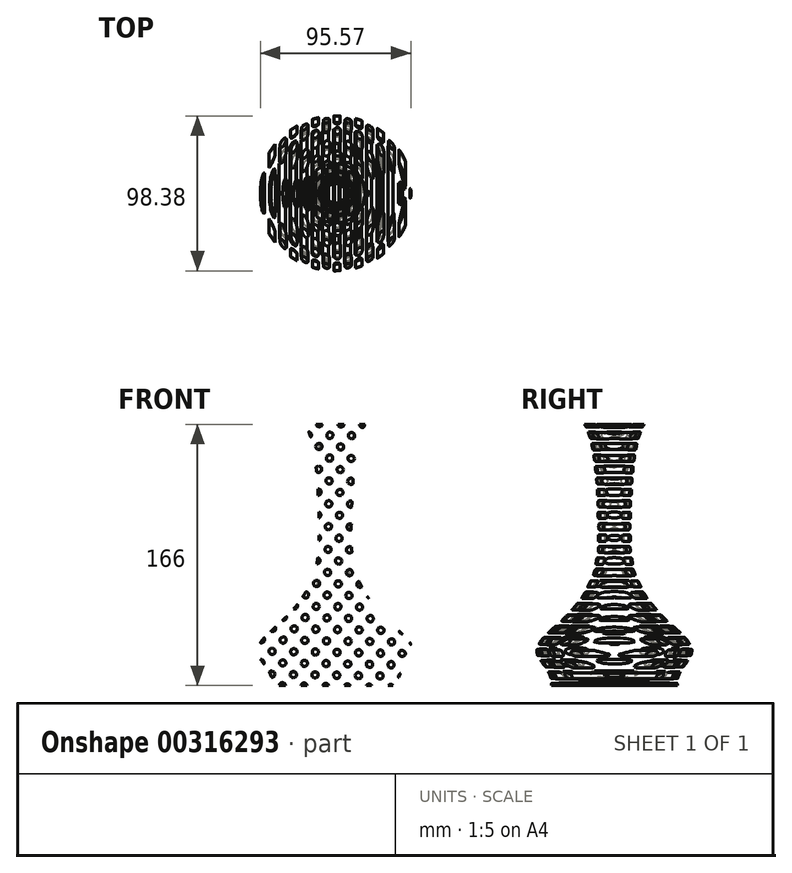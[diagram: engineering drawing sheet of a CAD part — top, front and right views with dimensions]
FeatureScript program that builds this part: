
annotation { "Feature Type Name" : "Feature", "Feature Type Description" : "" }
export const myFeature = defineFeature(function(context is Context, id is Id, definition is map)
    precondition{}
    {
        {
            var Q0;
            Q0=qCreatedBy(makeId("Top.planeOp"),FACE);
            var sketch = newSketch(context, id + "F0", { "sketchPlane" : qUnion([Q0])});
            skCircle(sketch, "E0", {"center": v(0, 0) * mm, "radius": 40 * mm});
            skSolve(sketch);
        }
        {
            var Q0;
            Q0=makeQuery(id+"F0.imprint","IMPRINT",FACE,{"disambiguationData":[TD([[makeQuery(id+"F0.imprint","IMPRINT",EDGE,{"derivedFrom":sQuery(id+"F0.wireOp",EDGE,"E0")}),1.0]])]});
            cPlane(context, id + "F1", {"entities" : qUnion([Q0]), "cplaneType" : CPlaneType.OFFSET, "offset" : 4 * mm, "width" : 150 * mm, "height" : 150 * mm});
        }
        {
            var Q0;
            Q0=qCreatedBy(id+"F1.planeOp",FACE);
            var sketch = newSketch(context, id + "F2", { "sketchPlane" : qUnion([Q0])});
            skCircle(sketch, "E1", {"center": v(0, 0) * mm, "radius": 41.51 * mm});
            skSolve(sketch);
        }
        {
            var Q0;
            Q0=makeQuery(id+"F2.imprint","IMPRINT",FACE,{"disambiguationData":[TD([[makeQuery(id+"F2.imprint","IMPRINT",EDGE,{"derivedFrom":sQuery(id+"F2.wireOp",EDGE,"E1")}),1.0]])]});
            cPlane(context, id + "F3", {"entities" : qUnion([Q0]), "cplaneType" : CPlaneType.OFFSET, "offset" : 6 * mm, "width" : 150 * mm, "height" : 150 * mm});
        }
        {
            var Q0;
            Q0=qCreatedBy(id+"F3.planeOp",FACE);
            var sketch = newSketch(context, id + "F4", { "sketchPlane" : qUnion([Q0])});
            skCircle(sketch, "E2", {"center": v(0, 0) * mm, "radius": 45.5 * mm});
            skSolve(sketch);
        }
        {
            var Q0;
            Q0=makeQuery(id+"F4.imprint","IMPRINT",FACE,{"disambiguationData":[TD([[makeQuery(id+"F4.imprint","IMPRINT",EDGE,{"derivedFrom":sQuery(id+"F4.wireOp",EDGE,"E2")}),1.0]])]});
            cPlane(context, id + "F5", {"entities" : qUnion([Q0]), "cplaneType" : CPlaneType.OFFSET, "offset" : 8 * mm, "width" : 150 * mm, "height" : 150 * mm});
        }
        {
            var Q0;
            Q0=qCreatedBy(id+"F5.planeOp",FACE);
            var sketch = newSketch(context, id + "F6", { "sketchPlane" : qUnion([Q0])});
            skCircle(sketch, "E3", {"center": v(0, 0) * mm, "radius": 49.2 * mm});
            skSolve(sketch);
        }
        {
            var Q0;
            Q0=makeQuery(id+"F6.imprint","IMPRINT",FACE,{"disambiguationData":[TD([[makeQuery(id+"F6.imprint","IMPRINT",EDGE,{"derivedFrom":sQuery(id+"F6.wireOp",EDGE,"E3")}),1.0]])]});
            cPlane(context, id + "F7", {"entities" : qUnion([Q0]), "cplaneType" : CPlaneType.OFFSET, "offset" : 6 * mm, "width" : 150 * mm, "height" : 150 * mm});
        }
        {
            var Q0;
            Q0=qCreatedBy(id+"F7.planeOp",FACE);
            var sketch = newSketch(context, id + "F8", { "sketchPlane" : qUnion([Q0])});
            skCircle(sketch, "E4", {"center": v(0, 0) * mm, "radius": 47 * mm});
            skSolve(sketch);
        }
        {
            var Q0;
            Q0=qCreatedBy(id+"F7.planeOp",FACE);
            cPlane(context, id + "F9", {"entities" : qUnion([Q0]), "cplaneType" : CPlaneType.OFFSET, "offset" : 6 * mm, "width" : 150 * mm, "height" : 150 * mm});
        }
        {
            var Q0;
            Q0=qCreatedBy(id+"F9.planeOp",FACE);
            var sketch = newSketch(context, id + "F10", { "sketchPlane" : qUnion([Q0])});
            skCircle(sketch, "E5", {"center": v(0, 0) * mm, "radius": 41.44 * mm});
            skSolve(sketch);
        }
        {
            var Q0;
            Q0=qCreatedBy(id+"F9.planeOp",FACE);
            cPlane(context, id + "F11", {"entities" : qUnion([Q0]), "cplaneType" : CPlaneType.OFFSET, "offset" : 16 * mm, "width" : 150 * mm, "height" : 150 * mm});
        }
        {
            var Q0;
            Q0=qCreatedBy(id+"F11.planeOp",FACE);
            var sketch = newSketch(context, id + "F12", { "sketchPlane" : qUnion([Q0])});
            skCircle(sketch, "E6", {"center": v(0, 0) * mm, "radius": 25.29 * mm});
            skSolve(sketch);
        }
        {
            var Q0;
            Q0=qCreatedBy(id+"F11.planeOp",FACE);
            cPlane(context, id + "F13", {"entities" : qUnion([Q0]), "cplaneType" : CPlaneType.OFFSET, "offset" : 25 * mm, "width" : 150 * mm, "height" : 150 * mm});
        }
        {
            var Q0;
            Q0=qCreatedBy(id+"F13.planeOp",FACE);
            var sketch = newSketch(context, id + "F14", { "sketchPlane" : qUnion([Q0])});
            skCircle(sketch, "E7", {"center": v(0, 0) * mm, "radius": 12.22 * mm});
            skSolve(sketch);
        }
        {
            var Q0;
            Q0=qCreatedBy(id+"F13.planeOp",FACE);
            cPlane(context, id + "F15", {"entities" : qUnion([Q0]), "cplaneType" : CPlaneType.OFFSET, "offset" : 25 * mm, "width" : 150 * mm, "height" : 150 * mm});
        }
        {
            var Q0;
            Q0=qCreatedBy(id+"F15.planeOp",FACE);
            var sketch = newSketch(context, id + "F16", { "sketchPlane" : qUnion([Q0])});
            skCircle(sketch, "E8", {"center": v(0, 0) * mm, "radius": 10.18 * mm});
            skSolve(sketch);
        }
        {
            var Q0;
            Q0=qCreatedBy(id+"F15.planeOp",FACE);
            cPlane(context, id + "F17", {"entities" : qUnion([Q0]), "cplaneType" : CPlaneType.OFFSET, "offset" : 25 * mm, "width" : 150 * mm, "height" : 150 * mm});
        }
        {
            var Q0;
            Q0=qCreatedBy(id+"F17.planeOp",FACE);
            var sketch = newSketch(context, id + "F18", { "sketchPlane" : qUnion([Q0])});
            skCircle(sketch, "E9", {"center": v(0, 0) * mm, "radius": 11 * mm});
            skSolve(sketch);
        }
        {
            var Q0;
            Q0=qCreatedBy(id+"F17.planeOp",FACE);
            cPlane(context, id + "F19", {"entities" : qUnion([Q0]), "cplaneType" : CPlaneType.OFFSET, "offset" : 25 * mm, "width" : 150 * mm, "height" : 150 * mm});
        }
        {
            var Q0;
            Q0=qCreatedBy(id+"F19.planeOp",FACE);
            var sketch = newSketch(context, id + "F20", { "sketchPlane" : qUnion([Q0])});
            skCircle(sketch, "E10", {"center": v(0, 0) * mm, "radius": 13.75 * mm});
            skSolve(sketch);
        }
        {
            var Q0;
            Q0=qCreatedBy(id+"F19.planeOp",FACE);
            cPlane(context, id + "F21", {"entities" : qUnion([Q0]), "cplaneType" : CPlaneType.OFFSET, "offset" : 10 * mm, "width" : 150 * mm, "height" : 150 * mm});
        }
        {
            var Q0;
            Q0=qCreatedBy(id+"F21.planeOp",FACE);
            var sketch = newSketch(context, id + "F22", { "sketchPlane" : qUnion([Q0])});
            skCircle(sketch, "E11", {"center": v(0, 0) * mm, "radius": 16.33 * mm});
            skSolve(sketch);
        }
        {
            var Q0;
            Q0=qCreatedBy(id+"F21.planeOp",FACE);
            cPlane(context, id + "F23", {"entities" : qUnion([Q0]), "cplaneType" : CPlaneType.OFFSET, "offset" : 6 * mm, "width" : 150 * mm, "height" : 150 * mm});
        }
        {
            var Q0;
            Q0=qCreatedBy(id+"F23.planeOp",FACE);
            var sketch = newSketch(context, id + "F24", { "sketchPlane" : qUnion([Q0])});
            skCircle(sketch, "E12", {"center": v(0, 0) * mm, "radius": 18.94 * mm});
            skSolve(sketch);
        }
        {
            var Q0;
            Q0=qSketchRegion(id+"F0",true);
            var Q1;
            Q1=qSketchRegion(id+"F2",true);
            var Q2;
            Q2=qSketchRegion(id+"F4",true);
            var Q3;
            Q3=qSketchRegion(id+"F6",true);
            var Q4;
            Q4=qSketchRegion(id+"F8",true);
            var Q5;
            Q5=qSketchRegion(id+"F10",true);
            var Q6;
            Q6=qSketchRegion(id+"F12",true);
            var Q7;
            Q7=qSketchRegion(id+"F14",true);
            var Q8;
            Q8=qSketchRegion(id+"F16",true);
            var Q9;
            Q9=qSketchRegion(id+"F18",true);
            var Q10;
            Q10=qSketchRegion(id+"F20",true);
            var Q11;
            Q11=qSketchRegion(id+"F22",true);
            var Q12;
            Q12=qSketchRegion(id+"F24",true);
            loft(context, id + "F25", {"sheetProfilesArray" : [{ "sheetProfileEntities" : qUnion([Q0]) }, { "sheetProfileEntities" : qUnion([Q1]) }, { "sheetProfileEntities" : qUnion([Q2]) }, { "sheetProfileEntities" : qUnion([Q3]) }, { "sheetProfileEntities" : qUnion([Q4]) }, { "sheetProfileEntities" : qUnion([Q5]) }, { "sheetProfileEntities" : qUnion([Q6]) }, { "sheetProfileEntities" : qUnion([Q7]) }, { "sheetProfileEntities" : qUnion([Q8]) }, { "sheetProfileEntities" : qUnion([Q9]) }, { "sheetProfileEntities" : qUnion([Q10]) }, { "sheetProfileEntities" : qUnion([Q11]) }, { "sheetProfileEntities" : qUnion([Q12]) }]});
        }
        {
            var Q0;
            Q0=makeQuery(id+"F25.opLoft","CAP_FACE",FACE,{"disambiguationData":[OSD([makeQuery(id+"F24.imprint","IMPRINT",FACE,{"disambiguationData":[TD([[makeQuery(id+"F24.imprint","IMPRINT",EDGE,{"derivedFrom":sQuery(id+"F24.wireOp",EDGE,"E12")}),1.0]])]})])],"isStart":true});
            shell(context, id + "F26", {"entities" : qUnion([Q0]), "thickness" : 4 * mm});
        }
        {
            var Q0;
            Q0=qCreatedBy(makeId("Top.planeOp"),FACE);
            var sketch = newSketch(context, id + "F27", { "sketchPlane" : qUnion([Q0])});
            skCircle(sketch, "E13", {"center": v(0, 0) * mm, "radius": 40.24 * mm});
            skSolve(sketch);
        }
        {
            var Q0;
            Q0=qSketchRegion(id+"F27",true);
            extrude(context, id + "F28", {"entities" : qUnion([Q0]), "operationType" : NewBodyOperationType.ADD, "oppositeDirection" : true, "depth" : 4 * mm});
        }
        {
            var Q0;
            Q0=qCreatedBy(makeId("Front.planeOp"),FACE);
            var sketch = newSketch(context, id + "F29", { "sketchPlane" : qUnion([Q0])});
            skCircle(sketch, "E14", {"center": v(0, -55.44) * mm, "radius": 2 * mm});
            skCircle(sketch, "E15.0.1.0", {"center": v(-6.76, -48.08) * mm, "radius": 2 * mm});
            skCircle(sketch, "E15.0.2.0", {"center": v(-13.52, -40.7) * mm, "radius": 2 * mm});
            skCircle(sketch, "E15.0.3.0", {"center": v(-20.28, -33.34) * mm, "radius": 2 * mm});
            skCircle(sketch, "E15.0.4.0", {"center": v(-27.04, -25.97) * mm, "radius": 2 * mm});
            skCircle(sketch, "E15.0.5.0", {"center": v(-33.8, -18.6) * mm, "radius": 2 * mm});
            skCircle(sketch, "E15.0.6.0", {"center": v(-40.56, -11.23) * mm, "radius": 2 * mm});
            skCircle(sketch, "E15.0.7.0", {"center": v(-47.32, -3.86) * mm, "radius": 2 * mm});
            skCircle(sketch, "E15.0.8.0", {"center": v(-54.07, 3.51) * mm, "radius": 2 * mm});
            skCircle(sketch, "E15.0.9.0", {"center": v(-60.83, 10.88) * mm, "radius": 2 * mm});
            skCircle(sketch, "E15.0.10.0", {"center": v(-67.6, 18.25) * mm, "radius": 2 * mm});
            skCircle(sketch, "E15.0.11.0", {"center": v(-74.35, 25.62) * mm, "radius": 2 * mm});
            skCircle(sketch, "E15.0.12.0", {"center": v(-81.11, 33) * mm, "radius": 2 * mm});
            skCircle(sketch, "E15.0.13.0", {"center": v(-87.87, 40.36) * mm, "radius": 2 * mm});
            skCircle(sketch, "E15.0.14.0", {"center": v(-94.63, 47.73) * mm, "radius": 2 * mm});
            skCircle(sketch, "E15.0.15.0", {"center": v(-101.39, 55.1) * mm, "radius": 2 * mm});
            skCircle(sketch, "E15.0.16.0", {"center": v(-108.15, 62.47) * mm, "radius": 2 * mm});
            skCircle(sketch, "E15.0.17.0", {"center": v(-114.9, 69.84) * mm, "radius": 2 * mm});
            skCircle(sketch, "E15.0.18.0", {"center": v(-121.67, 77.2) * mm, "radius": 2 * mm});
            skCircle(sketch, "E15.0.19.0", {"center": v(-128.43, 84.58) * mm, "radius": 2 * mm});
            skCircle(sketch, "E15.0.20.0", {"center": v(-135.19, 91.95) * mm, "radius": 2 * mm});
            skCircle(sketch, "E15.0.21.0", {"center": v(-141.95, 99.32) * mm, "radius": 2 * mm});
            skCircle(sketch, "E15.0.22.0", {"center": v(-148.7, 106.69) * mm, "radius": 2 * mm});
            skCircle(sketch, "E15.0.23.0", {"center": v(-155.46, 114.06) * mm, "radius": 2 * mm});
            skCircle(sketch, "E15.0.24.0", {"center": v(-162.22, 121.43) * mm, "radius": 2 * mm});
            skCircle(sketch, "E15.1.0.0", {"center": v(7, -48.3) * mm, "radius": 2 * mm});
            skCircle(sketch, "E15.1.1.0", {"center": v(0.24, -40.94) * mm, "radius": 2 * mm});
            skCircle(sketch, "E15.1.2.0", {"center": v(-6.52, -33.57) * mm, "radius": 2 * mm});
            skCircle(sketch, "E15.1.3.0", {"center": v(-13.27, -26.2) * mm, "radius": 2 * mm});
            skCircle(sketch, "E15.1.4.0", {"center": v(-20.03, -18.83) * mm, "radius": 2 * mm});
            skCircle(sketch, "E15.1.5.0", {"center": v(-26.8, -11.46) * mm, "radius": 2 * mm});
            skCircle(sketch, "E15.1.6.0", {"center": v(-33.55, -4.09) * mm, "radius": 2 * mm});
            skCircle(sketch, "E15.1.7.0", {"center": v(-40.31, 3.28) * mm, "radius": 2 * mm});
            skCircle(sketch, "E15.1.8.0", {"center": v(-47.07, 10.65) * mm, "radius": 2 * mm});
            skCircle(sketch, "E15.1.9.0", {"center": v(-53.83, 18.02) * mm, "radius": 2 * mm});
            skCircle(sketch, "E15.1.10.0", {"center": v(-60.6, 25.4) * mm, "radius": 2 * mm});
            skCircle(sketch, "E15.1.11.0", {"center": v(-67.35, 32.76) * mm, "radius": 2 * mm});
            skCircle(sketch, "E15.1.12.0", {"center": v(-74.1, 40.13) * mm, "radius": 2 * mm});
            skCircle(sketch, "E15.1.13.0", {"center": v(-80.87, 47.5) * mm, "radius": 2 * mm});
            skCircle(sketch, "E15.1.14.0", {"center": v(-87.63, 54.87) * mm, "radius": 2 * mm});
            skCircle(sketch, "E15.1.15.0", {"center": v(-94.39, 62.24) * mm, "radius": 2 * mm});
            skCircle(sketch, "E15.1.16.0", {"center": v(-101.15, 69.6) * mm, "radius": 2 * mm});
            skCircle(sketch, "E15.1.17.0", {"center": v(-107.9, 76.98) * mm, "radius": 2 * mm});
            skCircle(sketch, "E15.1.18.0", {"center": v(-114.66, 84.35) * mm, "radius": 2 * mm});
            skCircle(sketch, "E15.1.19.0", {"center": v(-121.42, 91.72) * mm, "radius": 2 * mm});
            skCircle(sketch, "E15.1.20.0", {"center": v(-128.18, 99.09) * mm, "radius": 2 * mm});
            skCircle(sketch, "E15.1.21.0", {"center": v(-134.94, 106.46) * mm, "radius": 2 * mm});
            skCircle(sketch, "E15.1.22.0", {"center": v(-141.7, 113.83) * mm, "radius": 2 * mm});
            skCircle(sketch, "E15.1.23.0", {"center": v(-148.46, 121.2) * mm, "radius": 2 * mm});
            skCircle(sketch, "E15.1.24.0", {"center": v(-155.22, 128.57) * mm, "radius": 2 * mm});
            skCircle(sketch, "E15.2.0.0", {"center": v(14, -41.17) * mm, "radius": 2 * mm});
            skCircle(sketch, "E15.2.1.0", {"center": v(7.25, -33.8) * mm, "radius": 2 * mm});
            skCircle(sketch, "E15.2.2.0", {"center": v(0.49, -26.43) * mm, "radius": 2 * mm});
            skCircle(sketch, "E15.2.3.0", {"center": v(-6.27, -19.06) * mm, "radius": 2 * mm});
            skCircle(sketch, "E15.2.4.0", {"center": v(-13.03, -11.69) * mm, "radius": 2 * mm});
            skCircle(sketch, "E15.2.5.0", {"center": v(-19.8, -4.32) * mm, "radius": 2 * mm});
            skCircle(sketch, "E15.2.6.0", {"center": v(-26.55, 3.05) * mm, "radius": 2 * mm});
            skCircle(sketch, "E15.2.7.0", {"center": v(-33.3, 10.42) * mm, "radius": 2 * mm});
            skCircle(sketch, "E15.2.8.0", {"center": v(-40.07, 17.79) * mm, "radius": 2 * mm});
            skCircle(sketch, "E15.2.9.0", {"center": v(-46.83, 25.16) * mm, "radius": 2 * mm});
            skCircle(sketch, "E15.2.10.0", {"center": v(-53.59, 32.53) * mm, "radius": 2 * mm});
            skCircle(sketch, "E15.2.11.0", {"center": v(-60.35, 39.9) * mm, "radius": 2 * mm});
            skCircle(sketch, "E15.2.12.0", {"center": v(-67.1, 47.27) * mm, "radius": 2 * mm});
            skCircle(sketch, "E15.2.13.0", {"center": v(-73.86, 54.64) * mm, "radius": 2 * mm});
            skCircle(sketch, "E15.2.14.0", {"center": v(-80.62, 62) * mm, "radius": 2 * mm});
            skCircle(sketch, "E15.2.15.0", {"center": v(-87.38, 69.38) * mm, "radius": 2 * mm});
            skCircle(sketch, "E15.2.16.0", {"center": v(-94.14, 76.75) * mm, "radius": 2 * mm});
            skCircle(sketch, "E15.2.17.0", {"center": v(-100.9, 84.12) * mm, "radius": 2 * mm});
            skCircle(sketch, "E15.2.18.0", {"center": v(-107.66, 91.49) * mm, "radius": 2 * mm});
            skCircle(sketch, "E15.2.19.0", {"center": v(-114.42, 98.86) * mm, "radius": 2 * mm});
            skCircle(sketch, "E15.2.20.0", {"center": v(-121.18, 106.23) * mm, "radius": 2 * mm});
            skCircle(sketch, "E15.2.21.0", {"center": v(-127.94, 113.6) * mm, "radius": 2 * mm});
            skCircle(sketch, "E15.2.22.0", {"center": v(-134.7, 120.96) * mm, "radius": 2 * mm});
            skCircle(sketch, "E15.2.23.0", {"center": v(-141.46, 128.33) * mm, "radius": 2 * mm});
            skCircle(sketch, "E15.2.24.0", {"center": v(-148.22, 135.7) * mm, "radius": 2 * mm});
            skCircle(sketch, "E15.3.0.0", {"center": v(21, -34.03) * mm, "radius": 2 * mm});
            skCircle(sketch, "E15.3.1.0", {"center": v(14.25, -26.66) * mm, "radius": 2 * mm});
            skCircle(sketch, "E15.3.2.0", {"center": v(7.5, -19.3) * mm, "radius": 2 * mm});
            skCircle(sketch, "E15.3.3.0", {"center": v(0.73, -11.92) * mm, "radius": 2 * mm});
            skCircle(sketch, "E15.3.4.0", {"center": v(-6.03, -4.55) * mm, "radius": 2 * mm});
            skCircle(sketch, "E15.3.5.0", {"center": v(-12.79, 2.82) * mm, "radius": 2 * mm});
            skCircle(sketch, "E15.3.6.0", {"center": v(-19.55, 10.19) * mm, "radius": 2 * mm});
            skCircle(sketch, "E15.3.7.0", {"center": v(-26.3, 17.56) * mm, "radius": 2 * mm});
            skCircle(sketch, "E15.3.8.0", {"center": v(-33.07, 24.93) * mm, "radius": 2 * mm});
            skCircle(sketch, "E15.3.9.0", {"center": v(-39.82, 32.3) * mm, "radius": 2 * mm});
            skCircle(sketch, "E15.3.10.0", {"center": v(-46.58, 39.67) * mm, "radius": 2 * mm});
            skCircle(sketch, "E15.3.11.0", {"center": v(-53.34, 47.04) * mm, "radius": 2 * mm});
            skCircle(sketch, "E15.3.12.0", {"center": v(-60.1, 54.4) * mm, "radius": 2 * mm});
            skCircle(sketch, "E15.3.13.0", {"center": v(-66.86, 61.78) * mm, "radius": 2 * mm});
            skCircle(sketch, "E15.3.14.0", {"center": v(-73.62, 69.15) * mm, "radius": 2 * mm});
            skCircle(sketch, "E15.3.15.0", {"center": v(-80.38, 76.52) * mm, "radius": 2 * mm});
            skCircle(sketch, "E15.3.16.0", {"center": v(-87.14, 83.89) * mm, "radius": 2 * mm});
            skCircle(sketch, "E15.3.17.0", {"center": v(-93.9, 91.25) * mm, "radius": 2 * mm});
            skCircle(sketch, "E15.3.18.0", {"center": v(-100.66, 98.62) * mm, "radius": 2 * mm});
            skCircle(sketch, "E15.3.19.0", {"center": v(-107.42, 106) * mm, "radius": 2 * mm});
            skCircle(sketch, "E15.3.20.0", {"center": v(-114.18, 113.36) * mm, "radius": 2 * mm});
            skCircle(sketch, "E15.3.21.0", {"center": v(-120.94, 120.73) * mm, "radius": 2 * mm});
            skCircle(sketch, "E15.3.22.0", {"center": v(-127.7, 128.1) * mm, "radius": 2 * mm});
            skCircle(sketch, "E15.3.23.0", {"center": v(-134.45, 135.47) * mm, "radius": 2 * mm});
            skCircle(sketch, "E15.3.24.0", {"center": v(-141.21, 142.84) * mm, "radius": 2 * mm});
            skCircle(sketch, "E15.4.0.0", {"center": v(28.01, -26.9) * mm, "radius": 2 * mm});
            skCircle(sketch, "E15.4.1.0", {"center": v(21.25, -19.52) * mm, "radius": 2 * mm});
            skCircle(sketch, "E15.4.2.0", {"center": v(14.5, -12.15) * mm, "radius": 2 * mm});
            skCircle(sketch, "E15.4.3.0", {"center": v(7.73, -4.78) * mm, "radius": 2 * mm});
            skCircle(sketch, "E15.4.4.0", {"center": v(0.97, 2.59) * mm, "radius": 2 * mm});
            skCircle(sketch, "E15.4.5.0", {"center": v(-5.78, 9.96) * mm, "radius": 2 * mm});
            skCircle(sketch, "E15.4.6.0", {"center": v(-12.54, 17.33) * mm, "radius": 2 * mm});
            skCircle(sketch, "E15.4.7.0", {"center": v(-19.3, 24.7) * mm, "radius": 2 * mm});
            skCircle(sketch, "E15.4.8.0", {"center": v(-26.06, 32.07) * mm, "radius": 2 * mm});
            skCircle(sketch, "E15.4.9.0", {"center": v(-32.82, 39.44) * mm, "radius": 2 * mm});
            skCircle(sketch, "E15.4.10.0", {"center": v(-39.58, 46.8) * mm, "radius": 2 * mm});
            skCircle(sketch, "E15.4.11.0", {"center": v(-46.34, 54.18) * mm, "radius": 2 * mm});
            skCircle(sketch, "E15.4.12.0", {"center": v(-53.1, 61.54) * mm, "radius": 2 * mm});
            skCircle(sketch, "E15.4.13.0", {"center": v(-59.86, 68.91) * mm, "radius": 2 * mm});
            skCircle(sketch, "E15.4.14.0", {"center": v(-66.62, 76.28) * mm, "radius": 2 * mm});
            skCircle(sketch, "E15.4.15.0", {"center": v(-73.38, 83.65) * mm, "radius": 2 * mm});
            skCircle(sketch, "E15.4.16.0", {"center": v(-80.14, 91.02) * mm, "radius": 2 * mm});
            skCircle(sketch, "E15.4.17.0", {"center": v(-86.9, 98.4) * mm, "radius": 2 * mm});
            skCircle(sketch, "E15.4.18.0", {"center": v(-93.66, 105.76) * mm, "radius": 2 * mm});
            skCircle(sketch, "E15.4.19.0", {"center": v(-100.41, 113.13) * mm, "radius": 2 * mm});
            skCircle(sketch, "E15.4.20.0", {"center": v(-107.17, 120.5) * mm, "radius": 2 * mm});
            skCircle(sketch, "E15.4.21.0", {"center": v(-113.93, 127.87) * mm, "radius": 2 * mm});
            skCircle(sketch, "E15.4.22.0", {"center": v(-120.7, 135.24) * mm, "radius": 2 * mm});
            skCircle(sketch, "E15.4.23.0", {"center": v(-127.45, 142.61) * mm, "radius": 2 * mm});
            skCircle(sketch, "E15.4.24.0", {"center": v(-134.21, 149.98) * mm, "radius": 2 * mm});
            skCircle(sketch, "E15.5.0.0", {"center": v(35.02, -19.75) * mm, "radius": 2 * mm});
            skCircle(sketch, "E15.5.1.0", {"center": v(28.26, -12.38) * mm, "radius": 2 * mm});
            skCircle(sketch, "E15.5.2.0", {"center": v(21.5, -5.01) * mm, "radius": 2 * mm});
            skCircle(sketch, "E15.5.3.0", {"center": v(14.74, 2.36) * mm, "radius": 2 * mm});
            skCircle(sketch, "E15.5.4.0", {"center": v(7.98, 9.73) * mm, "radius": 2 * mm});
            skCircle(sketch, "E15.5.5.0", {"center": v(1.22, 17.1) * mm, "radius": 2 * mm});
            skCircle(sketch, "E15.5.6.0", {"center": v(-5.54, 24.47) * mm, "radius": 2 * mm});
            skCircle(sketch, "E15.5.7.0", {"center": v(-12.3, 31.84) * mm, "radius": 2 * mm});
            skCircle(sketch, "E15.5.8.0", {"center": v(-19.06, 39.2) * mm, "radius": 2 * mm});
            skCircle(sketch, "E15.5.9.0", {"center": v(-25.82, 46.57) * mm, "radius": 2 * mm});
            skCircle(sketch, "E15.5.10.0", {"center": v(-32.58, 53.94) * mm, "radius": 2 * mm});
            skCircle(sketch, "E15.5.11.0", {"center": v(-39.34, 61.31) * mm, "radius": 2 * mm});
            skCircle(sketch, "E15.5.12.0", {"center": v(-46.1, 68.68) * mm, "radius": 2 * mm});
            skCircle(sketch, "E15.5.13.0", {"center": v(-52.86, 76.05) * mm, "radius": 2 * mm});
            skCircle(sketch, "E15.5.14.0", {"center": v(-59.62, 83.42) * mm, "radius": 2 * mm});
            skCircle(sketch, "E15.5.15.0", {"center": v(-66.37, 90.8) * mm, "radius": 2 * mm});
            skCircle(sketch, "E15.5.16.0", {"center": v(-73.13, 98.16) * mm, "radius": 2 * mm});
            skCircle(sketch, "E15.5.17.0", {"center": v(-79.9, 105.53) * mm, "radius": 2 * mm});
            skCircle(sketch, "E15.5.18.0", {"center": v(-86.65, 112.9) * mm, "radius": 2 * mm});
            skCircle(sketch, "E15.5.19.0", {"center": v(-93.41, 120.27) * mm, "radius": 2 * mm});
            skCircle(sketch, "E15.5.20.0", {"center": v(-100.17, 127.64) * mm, "radius": 2 * mm});
            skCircle(sketch, "E15.5.21.0", {"center": v(-106.93, 135.01) * mm, "radius": 2 * mm});
            skCircle(sketch, "E15.5.22.0", {"center": v(-113.69, 142.38) * mm, "radius": 2 * mm});
            skCircle(sketch, "E15.5.23.0", {"center": v(-120.45, 149.75) * mm, "radius": 2 * mm});
            skCircle(sketch, "E15.5.24.0", {"center": v(-127.2, 157.12) * mm, "radius": 2 * mm});
            skCircle(sketch, "E15.6.0.0", {"center": v(42.02, -12.61) * mm, "radius": 2 * mm});
            skCircle(sketch, "E15.6.1.0", {"center": v(35.26, -5.24) * mm, "radius": 2 * mm});
            skCircle(sketch, "E15.6.2.0", {"center": v(28.5, 2.13) * mm, "radius": 2 * mm});
            skCircle(sketch, "E15.6.3.0", {"center": v(21.74, 9.5) * mm, "radius": 2 * mm});
            skCircle(sketch, "E15.6.4.0", {"center": v(14.98, 16.86) * mm, "radius": 2 * mm});
            skCircle(sketch, "E15.6.5.0", {"center": v(8.22, 24.23) * mm, "radius": 2 * mm});
            skCircle(sketch, "E15.6.6.0", {"center": v(1.46, 31.6) * mm, "radius": 2 * mm});
            skCircle(sketch, "E15.6.7.0", {"center": v(-5.3, 38.97) * mm, "radius": 2 * mm});
            skCircle(sketch, "E15.6.8.0", {"center": v(-12.06, 46.34) * mm, "radius": 2 * mm});
            skCircle(sketch, "E15.6.9.0", {"center": v(-18.82, 53.71) * mm, "radius": 2 * mm});
            skCircle(sketch, "E15.6.10.0", {"center": v(-25.57, 61.08) * mm, "radius": 2 * mm});
            skCircle(sketch, "E15.6.11.0", {"center": v(-32.33, 68.45) * mm, "radius": 2 * mm});
            skCircle(sketch, "E15.6.12.0", {"center": v(-39.1, 75.82) * mm, "radius": 2 * mm});
            skCircle(sketch, "E15.6.13.0", {"center": v(-45.85, 83.2) * mm, "radius": 2 * mm});
            skCircle(sketch, "E15.6.14.0", {"center": v(-52.61, 90.56) * mm, "radius": 2 * mm});
            skCircle(sketch, "E15.6.15.0", {"center": v(-59.37, 97.93) * mm, "radius": 2 * mm});
            skCircle(sketch, "E15.6.16.0", {"center": v(-66.13, 105.3) * mm, "radius": 2 * mm});
            skCircle(sketch, "E15.6.17.0", {"center": v(-72.9, 112.67) * mm, "radius": 2 * mm});
            skCircle(sketch, "E15.6.18.0", {"center": v(-79.65, 120.04) * mm, "radius": 2 * mm});
            skCircle(sketch, "E15.6.19.0", {"center": v(-86.4, 127.4) * mm, "radius": 2 * mm});
            skCircle(sketch, "E15.6.20.0", {"center": v(-93.17, 134.78) * mm, "radius": 2 * mm});
            skCircle(sketch, "E15.6.21.0", {"center": v(-99.93, 142.15) * mm, "radius": 2 * mm});
            skCircle(sketch, "E15.6.22.0", {"center": v(-106.69, 149.52) * mm, "radius": 2 * mm});
            skCircle(sketch, "E15.6.23.0", {"center": v(-113.45, 156.89) * mm, "radius": 2 * mm});
            skCircle(sketch, "E15.6.24.0", {"center": v(-120.2, 164.26) * mm, "radius": 2 * mm});
            skCircle(sketch, "E15.7.0.0", {"center": v(49.02, -5.48) * mm, "radius": 2 * mm});
            skCircle(sketch, "E15.7.1.0", {"center": v(42.26, 1.9) * mm, "radius": 2 * mm});
            skCircle(sketch, "E15.7.2.0", {"center": v(35.5, 9.26) * mm, "radius": 2 * mm});
            skCircle(sketch, "E15.7.3.0", {"center": v(28.74, 16.63) * mm, "radius": 2 * mm});
            skCircle(sketch, "E15.7.4.0", {"center": v(21.98, 24) * mm, "radius": 2 * mm});
            skCircle(sketch, "E15.7.5.0", {"center": v(15.22, 31.37) * mm, "radius": 2 * mm});
            skCircle(sketch, "E15.7.6.0", {"center": v(8.47, 38.74) * mm, "radius": 2 * mm});
            skCircle(sketch, "E15.7.7.0", {"center": v(1.7, 46.11) * mm, "radius": 2 * mm});
            skCircle(sketch, "E15.7.8.0", {"center": v(-5.05, 53.48) * mm, "radius": 2 * mm});
            skCircle(sketch, "E15.7.9.0", {"center": v(-11.81, 60.85) * mm, "radius": 2 * mm});
            skCircle(sketch, "E15.7.10.0", {"center": v(-18.57, 68.22) * mm, "radius": 2 * mm});
            skCircle(sketch, "E15.7.11.0", {"center": v(-25.33, 75.6) * mm, "radius": 2 * mm});
            skCircle(sketch, "E15.7.12.0", {"center": v(-32.1, 82.96) * mm, "radius": 2 * mm});
            skCircle(sketch, "E15.7.13.0", {"center": v(-38.85, 90.33) * mm, "radius": 2 * mm});
            skCircle(sketch, "E15.7.14.0", {"center": v(-45.6, 97.7) * mm, "radius": 2 * mm});
            skCircle(sketch, "E15.7.15.0", {"center": v(-52.37, 105.07) * mm, "radius": 2 * mm});
            skCircle(sketch, "E15.7.16.0", {"center": v(-59.13, 112.44) * mm, "radius": 2 * mm});
            skCircle(sketch, "E15.7.17.0", {"center": v(-65.89, 119.8) * mm, "radius": 2 * mm});
            skCircle(sketch, "E15.7.18.0", {"center": v(-72.65, 127.18) * mm, "radius": 2 * mm});
            skCircle(sketch, "E15.7.19.0", {"center": v(-79.4, 134.55) * mm, "radius": 2 * mm});
            skCircle(sketch, "E15.7.20.0", {"center": v(-86.16, 141.92) * mm, "radius": 2 * mm});
            skCircle(sketch, "E15.7.21.0", {"center": v(-92.92, 149.29) * mm, "radius": 2 * mm});
            skCircle(sketch, "E15.7.22.0", {"center": v(-99.68, 156.66) * mm, "radius": 2 * mm});
            skCircle(sketch, "E15.7.23.0", {"center": v(-106.44, 164.03) * mm, "radius": 2 * mm});
            skCircle(sketch, "E15.7.24.0", {"center": v(-113.2, 171.4) * mm, "radius": 2 * mm});
            skCircle(sketch, "E15.8.0.0", {"center": v(56.02, 1.66) * mm, "radius": 2 * mm});
            skCircle(sketch, "E15.8.1.0", {"center": v(49.26, 9.03) * mm, "radius": 2 * mm});
            skCircle(sketch, "E15.8.2.0", {"center": v(42.5, 16.4) * mm, "radius": 2 * mm});
            skCircle(sketch, "E15.8.3.0", {"center": v(35.75, 23.77) * mm, "radius": 2 * mm});
            skCircle(sketch, "E15.8.4.0", {"center": v(28.99, 31.14) * mm, "radius": 2 * mm});
            skCircle(sketch, "E15.8.5.0", {"center": v(22.23, 38.51) * mm, "radius": 2 * mm});
            skCircle(sketch, "E15.8.6.0", {"center": v(15.47, 45.88) * mm, "radius": 2 * mm});
            skCircle(sketch, "E15.8.7.0", {"center": v(8.7, 53.25) * mm, "radius": 2 * mm});
            skCircle(sketch, "E15.8.8.0", {"center": v(1.95, 60.62) * mm, "radius": 2 * mm});
            skCircle(sketch, "E15.8.9.0", {"center": v(-4.8, 67.99) * mm, "radius": 2 * mm});
            skCircle(sketch, "E15.8.10.0", {"center": v(-11.57, 75.36) * mm, "radius": 2 * mm});
            skCircle(sketch, "E15.8.11.0", {"center": v(-18.33, 82.73) * mm, "radius": 2 * mm});
            skCircle(sketch, "E15.8.12.0", {"center": v(-25.09, 90.1) * mm, "radius": 2 * mm});
            skCircle(sketch, "E15.8.13.0", {"center": v(-31.85, 97.47) * mm, "radius": 2 * mm});
            skCircle(sketch, "E15.8.14.0", {"center": v(-38.6, 104.84) * mm, "radius": 2 * mm});
            skCircle(sketch, "E15.8.15.0", {"center": v(-45.37, 112.2) * mm, "radius": 2 * mm});
            skCircle(sketch, "E15.8.16.0", {"center": v(-52.12, 119.58) * mm, "radius": 2 * mm});
            skCircle(sketch, "E15.8.17.0", {"center": v(-58.88, 126.95) * mm, "radius": 2 * mm});
            skCircle(sketch, "E15.8.18.0", {"center": v(-65.64, 134.32) * mm, "radius": 2 * mm});
            skCircle(sketch, "E15.8.19.0", {"center": v(-72.4, 141.69) * mm, "radius": 2 * mm});
            skCircle(sketch, "E15.8.20.0", {"center": v(-79.16, 149.06) * mm, "radius": 2 * mm});
            skCircle(sketch, "E15.8.21.0", {"center": v(-85.92, 156.43) * mm, "radius": 2 * mm});
            skCircle(sketch, "E15.8.22.0", {"center": v(-92.68, 163.8) * mm, "radius": 2 * mm});
            skCircle(sketch, "E15.8.23.0", {"center": v(-99.44, 171.16) * mm, "radius": 2 * mm});
            skCircle(sketch, "E15.8.24.0", {"center": v(-106.2, 178.53) * mm, "radius": 2 * mm});
            skCircle(sketch, "E15.9.0.0", {"center": v(63.03, 8.8) * mm, "radius": 2 * mm});
            skCircle(sketch, "E15.9.1.0", {"center": v(56.27, 16.17) * mm, "radius": 2 * mm});
            skCircle(sketch, "E15.9.2.0", {"center": v(49.5, 23.54) * mm, "radius": 2 * mm});
            skCircle(sketch, "E15.9.3.0", {"center": v(42.75, 30.91) * mm, "radius": 2 * mm});
            skCircle(sketch, "E15.9.4.0", {"center": v(36, 38.28) * mm, "radius": 2 * mm});
            skCircle(sketch, "E15.9.5.0", {"center": v(29.23, 45.65) * mm, "radius": 2 * mm});
            skCircle(sketch, "E15.9.6.0", {"center": v(22.47, 53.02) * mm, "radius": 2 * mm});
            skCircle(sketch, "E15.9.7.0", {"center": v(15.71, 60.39) * mm, "radius": 2 * mm});
            skCircle(sketch, "E15.9.8.0", {"center": v(8.95, 67.76) * mm, "radius": 2 * mm});
            skCircle(sketch, "E15.9.9.0", {"center": v(2.2, 75.13) * mm, "radius": 2 * mm});
            skCircle(sketch, "E15.9.10.0", {"center": v(-4.57, 82.5) * mm, "radius": 2 * mm});
            skCircle(sketch, "E15.9.11.0", {"center": v(-11.33, 89.87) * mm, "radius": 2 * mm});
            skCircle(sketch, "E15.9.12.0", {"center": v(-18.08, 97.24) * mm, "radius": 2 * mm});
            skCircle(sketch, "E15.9.13.0", {"center": v(-24.84, 104.6) * mm, "radius": 2 * mm});
            skCircle(sketch, "E15.9.14.0", {"center": v(-31.6, 111.98) * mm, "radius": 2 * mm});
            skCircle(sketch, "E15.9.15.0", {"center": v(-38.36, 119.35) * mm, "radius": 2 * mm});
            skCircle(sketch, "E15.9.16.0", {"center": v(-45.12, 126.72) * mm, "radius": 2 * mm});
            skCircle(sketch, "E15.9.17.0", {"center": v(-51.88, 134.09) * mm, "radius": 2 * mm});
            skCircle(sketch, "E15.9.18.0", {"center": v(-58.64, 141.46) * mm, "radius": 2 * mm});
            skCircle(sketch, "E15.9.19.0", {"center": v(-65.4, 148.82) * mm, "radius": 2 * mm});
            skCircle(sketch, "E15.9.20.0", {"center": v(-72.16, 156.2) * mm, "radius": 2 * mm});
            skCircle(sketch, "E15.9.21.0", {"center": v(-78.92, 163.56) * mm, "radius": 2 * mm});
            skCircle(sketch, "E15.9.22.0", {"center": v(-85.68, 170.93) * mm, "radius": 2 * mm});
            skCircle(sketch, "E15.9.23.0", {"center": v(-92.44, 178.3) * mm, "radius": 2 * mm});
            skCircle(sketch, "E15.9.24.0", {"center": v(-99.2, 185.67) * mm, "radius": 2 * mm});
            skCircle(sketch, "E15.10.0.0", {"center": v(70.03, 15.94) * mm, "radius": 2 * mm});
            skCircle(sketch, "E15.10.1.0", {"center": v(63.27, 23.3) * mm, "radius": 2 * mm});
            skCircle(sketch, "E15.10.2.0", {"center": v(56.51, 30.68) * mm, "radius": 2 * mm});
            skCircle(sketch, "E15.10.3.0", {"center": v(49.75, 38.05) * mm, "radius": 2 * mm});
            skCircle(sketch, "E15.10.4.0", {"center": v(43, 45.42) * mm, "radius": 2 * mm});
            skCircle(sketch, "E15.10.5.0", {"center": v(36.23, 52.79) * mm, "radius": 2 * mm});
            skCircle(sketch, "E15.10.6.0", {"center": v(29.47, 60.16) * mm, "radius": 2 * mm});
            skCircle(sketch, "E15.10.7.0", {"center": v(22.72, 67.53) * mm, "radius": 2 * mm});
            skCircle(sketch, "E15.10.8.0", {"center": v(15.96, 74.9) * mm, "radius": 2 * mm});
            skCircle(sketch, "E15.10.9.0", {"center": v(9.2, 82.27) * mm, "radius": 2 * mm});
            skCircle(sketch, "E15.10.10.0", {"center": v(2.44, 89.64) * mm, "radius": 2 * mm});
            skCircle(sketch, "E15.10.11.0", {"center": v(-4.32, 97) * mm, "radius": 2 * mm});
            skCircle(sketch, "E15.10.12.0", {"center": v(-11.08, 104.38) * mm, "radius": 2 * mm});
            skCircle(sketch, "E15.10.13.0", {"center": v(-17.84, 111.75) * mm, "radius": 2 * mm});
            skCircle(sketch, "E15.10.14.0", {"center": v(-24.6, 119.11) * mm, "radius": 2 * mm});
            skCircle(sketch, "E15.10.15.0", {"center": v(-31.36, 126.48) * mm, "radius": 2 * mm});
            skCircle(sketch, "E15.10.16.0", {"center": v(-38.12, 133.85) * mm, "radius": 2 * mm});
            skCircle(sketch, "E15.10.17.0", {"center": v(-44.88, 141.22) * mm, "radius": 2 * mm});
            skCircle(sketch, "E15.10.18.0", {"center": v(-51.64, 148.6) * mm, "radius": 2 * mm});
            skCircle(sketch, "E15.10.19.0", {"center": v(-58.4, 155.96) * mm, "radius": 2 * mm});
            skCircle(sketch, "E15.10.20.0", {"center": v(-65.16, 163.33) * mm, "radius": 2 * mm});
            skCircle(sketch, "E15.10.21.0", {"center": v(-71.92, 170.7) * mm, "radius": 2 * mm});
            skCircle(sketch, "E15.10.22.0", {"center": v(-78.67, 178.07) * mm, "radius": 2 * mm});
            skCircle(sketch, "E15.10.23.0", {"center": v(-85.43, 185.44) * mm, "radius": 2 * mm});
            skCircle(sketch, "E15.10.24.0", {"center": v(-92.2, 192.81) * mm, "radius": 2 * mm});
            skCircle(sketch, "E15.11.0.0", {"center": v(77.03, 23.08) * mm, "radius": 2 * mm});
            skCircle(sketch, "E15.11.1.0", {"center": v(70.27, 30.45) * mm, "radius": 2 * mm});
            skCircle(sketch, "E15.11.2.0", {"center": v(63.51, 37.82) * mm, "radius": 2 * mm});
            skCircle(sketch, "E15.11.3.0", {"center": v(56.76, 45.19) * mm, "radius": 2 * mm});
            skCircle(sketch, "E15.11.4.0", {"center": v(50, 52.56) * mm, "radius": 2 * mm});
            skCircle(sketch, "E15.11.5.0", {"center": v(43.24, 59.93) * mm, "radius": 2 * mm});
            skCircle(sketch, "E15.11.6.0", {"center": v(36.48, 67.3) * mm, "radius": 2 * mm});
            skCircle(sketch, "E15.11.7.0", {"center": v(29.72, 74.67) * mm, "radius": 2 * mm});
            skCircle(sketch, "E15.11.8.0", {"center": v(22.96, 82.04) * mm, "radius": 2 * mm});
            skCircle(sketch, "E15.11.9.0", {"center": v(16.2, 89.4) * mm, "radius": 2 * mm});
            skCircle(sketch, "E15.11.10.0", {"center": v(9.44, 96.77) * mm, "radius": 2 * mm});
            skCircle(sketch, "E15.11.11.0", {"center": v(2.68, 104.14) * mm, "radius": 2 * mm});
            skCircle(sketch, "E15.11.12.0", {"center": v(-4.08, 111.51) * mm, "radius": 2 * mm});
            skCircle(sketch, "E15.11.13.0", {"center": v(-10.84, 118.88) * mm, "radius": 2 * mm});
            skCircle(sketch, "E15.11.14.0", {"center": v(-17.6, 126.25) * mm, "radius": 2 * mm});
            skCircle(sketch, "E15.11.15.0", {"center": v(-24.36, 133.62) * mm, "radius": 2 * mm});
            skCircle(sketch, "E15.11.16.0", {"center": v(-31.12, 141) * mm, "radius": 2 * mm});
            skCircle(sketch, "E15.11.17.0", {"center": v(-37.87, 148.36) * mm, "radius": 2 * mm});
            skCircle(sketch, "E15.11.18.0", {"center": v(-44.63, 155.73) * mm, "radius": 2 * mm});
            skCircle(sketch, "E15.11.19.0", {"center": v(-51.4, 163.1) * mm, "radius": 2 * mm});
            skCircle(sketch, "E15.11.20.0", {"center": v(-58.15, 170.47) * mm, "radius": 2 * mm});
            skCircle(sketch, "E15.11.21.0", {"center": v(-64.91, 177.84) * mm, "radius": 2 * mm});
            skCircle(sketch, "E15.11.22.0", {"center": v(-71.67, 185.21) * mm, "radius": 2 * mm});
            skCircle(sketch, "E15.11.23.0", {"center": v(-78.43, 192.58) * mm, "radius": 2 * mm});
            skCircle(sketch, "E15.11.24.0", {"center": v(-85.2, 199.95) * mm, "radius": 2 * mm});
            skCircle(sketch, "E15.12.0.0", {"center": v(84.04, 30.22) * mm, "radius": 2 * mm});
            skCircle(sketch, "E15.12.1.0", {"center": v(77.28, 37.59) * mm, "radius": 2 * mm});
            skCircle(sketch, "E15.12.2.0", {"center": v(70.52, 44.96) * mm, "radius": 2 * mm});
            skCircle(sketch, "E15.12.3.0", {"center": v(63.76, 52.33) * mm, "radius": 2 * mm});
            skCircle(sketch, "E15.12.4.0", {"center": v(57, 59.7) * mm, "radius": 2 * mm});
            skCircle(sketch, "E15.12.5.0", {"center": v(50.24, 67.06) * mm, "radius": 2 * mm});
            skCircle(sketch, "E15.12.6.0", {"center": v(43.48, 74.43) * mm, "radius": 2 * mm});
            skCircle(sketch, "E15.12.7.0", {"center": v(36.72, 81.8) * mm, "radius": 2 * mm});
            skCircle(sketch, "E15.12.8.0", {"center": v(29.96, 89.17) * mm, "radius": 2 * mm});
            skCircle(sketch, "E15.12.9.0", {"center": v(23.2, 96.54) * mm, "radius": 2 * mm});
            skCircle(sketch, "E15.12.10.0", {"center": v(16.44, 103.91) * mm, "radius": 2 * mm});
            skCircle(sketch, "E15.12.11.0", {"center": v(9.68, 111.28) * mm, "radius": 2 * mm});
            skCircle(sketch, "E15.12.12.0", {"center": v(2.92, 118.65) * mm, "radius": 2 * mm});
            skCircle(sketch, "E15.12.13.0", {"center": v(-3.83, 126.02) * mm, "radius": 2 * mm});
            skCircle(sketch, "E15.12.14.0", {"center": v(-10.6, 133.4) * mm, "radius": 2 * mm});
            skCircle(sketch, "E15.12.15.0", {"center": v(-17.35, 140.76) * mm, "radius": 2 * mm});
            skCircle(sketch, "E15.12.16.0", {"center": v(-24.11, 148.13) * mm, "radius": 2 * mm});
            skCircle(sketch, "E15.12.17.0", {"center": v(-30.87, 155.5) * mm, "radius": 2 * mm});
            skCircle(sketch, "E15.12.18.0", {"center": v(-37.63, 162.87) * mm, "radius": 2 * mm});
            skCircle(sketch, "E15.12.19.0", {"center": v(-44.4, 170.24) * mm, "radius": 2 * mm});
            skCircle(sketch, "E15.12.20.0", {"center": v(-51.15, 177.6) * mm, "radius": 2 * mm});
            skCircle(sketch, "E15.12.21.0", {"center": v(-57.9, 184.98) * mm, "radius": 2 * mm});
            skCircle(sketch, "E15.12.22.0", {"center": v(-64.67, 192.35) * mm, "radius": 2 * mm});
            skCircle(sketch, "E15.12.23.0", {"center": v(-71.43, 199.72) * mm, "radius": 2 * mm});
            skCircle(sketch, "E15.12.24.0", {"center": v(-78.19, 207.09) * mm, "radius": 2 * mm});
            skCircle(sketch, "E15.13.0.0", {"center": v(91.04, 37.36) * mm, "radius": 2 * mm});
            skCircle(sketch, "E15.13.1.0", {"center": v(84.28, 44.72) * mm, "radius": 2 * mm});
            skCircle(sketch, "E15.13.2.0", {"center": v(77.52, 52.1) * mm, "radius": 2 * mm});
            skCircle(sketch, "E15.13.3.0", {"center": v(70.76, 59.46) * mm, "radius": 2 * mm});
            skCircle(sketch, "E15.13.4.0", {"center": v(64, 66.83) * mm, "radius": 2 * mm});
            skCircle(sketch, "E15.13.5.0", {"center": v(57.24, 74.2) * mm, "radius": 2 * mm});
            skCircle(sketch, "E15.13.6.0", {"center": v(50.48, 81.57) * mm, "radius": 2 * mm});
            skCircle(sketch, "E15.13.7.0", {"center": v(43.72, 88.94) * mm, "radius": 2 * mm});
            skCircle(sketch, "E15.13.8.0", {"center": v(36.96, 96.31) * mm, "radius": 2 * mm});
            skCircle(sketch, "E15.13.9.0", {"center": v(30.2, 103.68) * mm, "radius": 2 * mm});
            skCircle(sketch, "E15.13.10.0", {"center": v(23.45, 111.05) * mm, "radius": 2 * mm});
            skCircle(sketch, "E15.13.11.0", {"center": v(16.69, 118.42) * mm, "radius": 2 * mm});
            skCircle(sketch, "E15.13.12.0", {"center": v(9.93, 125.8) * mm, "radius": 2 * mm});
            skCircle(sketch, "E15.13.13.0", {"center": v(3.17, 133.16) * mm, "radius": 2 * mm});
            skCircle(sketch, "E15.13.14.0", {"center": v(-3.6, 140.53) * mm, "radius": 2 * mm});
            skCircle(sketch, "E15.13.15.0", {"center": v(-10.35, 147.9) * mm, "radius": 2 * mm});
            skCircle(sketch, "E15.13.16.0", {"center": v(-17.1, 155.27) * mm, "radius": 2 * mm});
            skCircle(sketch, "E15.13.17.0", {"center": v(-23.87, 162.64) * mm, "radius": 2 * mm});
            skCircle(sketch, "E15.13.18.0", {"center": v(-30.63, 170) * mm, "radius": 2 * mm});
            skCircle(sketch, "E15.13.19.0", {"center": v(-37.39, 177.38) * mm, "radius": 2 * mm});
            skCircle(sketch, "E15.13.20.0", {"center": v(-44.15, 184.75) * mm, "radius": 2 * mm});
            skCircle(sketch, "E15.13.21.0", {"center": v(-50.9, 192.12) * mm, "radius": 2 * mm});
            skCircle(sketch, "E15.13.22.0", {"center": v(-57.67, 199.49) * mm, "radius": 2 * mm});
            skCircle(sketch, "E15.13.23.0", {"center": v(-64.42, 206.86) * mm, "radius": 2 * mm});
            skCircle(sketch, "E15.13.24.0", {"center": v(-71.18, 214.23) * mm, "radius": 2 * mm});
            skCircle(sketch, "E15.14.0.0", {"center": v(98.04, 44.5) * mm, "radius": 2 * mm});
            skCircle(sketch, "E15.14.1.0", {"center": v(91.28, 51.86) * mm, "radius": 2 * mm});
            skCircle(sketch, "E15.14.2.0", {"center": v(84.52, 59.23) * mm, "radius": 2 * mm});
            skCircle(sketch, "E15.14.3.0", {"center": v(77.76, 66.6) * mm, "radius": 2 * mm});
            skCircle(sketch, "E15.14.4.0", {"center": v(71, 73.97) * mm, "radius": 2 * mm});
            skCircle(sketch, "E15.14.5.0", {"center": v(64.25, 81.34) * mm, "radius": 2 * mm});
            skCircle(sketch, "E15.14.6.0", {"center": v(57.49, 88.71) * mm, "radius": 2 * mm});
            skCircle(sketch, "E15.14.7.0", {"center": v(50.73, 96.08) * mm, "radius": 2 * mm});
            skCircle(sketch, "E15.14.8.0", {"center": v(43.97, 103.45) * mm, "radius": 2 * mm});
            skCircle(sketch, "E15.14.9.0", {"center": v(37.2, 110.82) * mm, "radius": 2 * mm});
            skCircle(sketch, "E15.14.10.0", {"center": v(30.45, 118.2) * mm, "radius": 2 * mm});
            skCircle(sketch, "E15.14.11.0", {"center": v(23.7, 125.56) * mm, "radius": 2 * mm});
            skCircle(sketch, "E15.14.12.0", {"center": v(16.93, 132.93) * mm, "radius": 2 * mm});
            skCircle(sketch, "E15.14.13.0", {"center": v(10.17, 140.3) * mm, "radius": 2 * mm});
            skCircle(sketch, "E15.14.14.0", {"center": v(3.41, 147.67) * mm, "radius": 2 * mm});
            skCircle(sketch, "E15.14.15.0", {"center": v(-3.35, 155.04) * mm, "radius": 2 * mm});
            skCircle(sketch, "E15.14.16.0", {"center": v(-10.1, 162.4) * mm, "radius": 2 * mm});
            skCircle(sketch, "E15.14.17.0", {"center": v(-16.87, 169.78) * mm, "radius": 2 * mm});
            skCircle(sketch, "E15.14.18.0", {"center": v(-23.63, 177.15) * mm, "radius": 2 * mm});
            skCircle(sketch, "E15.14.19.0", {"center": v(-30.38, 184.52) * mm, "radius": 2 * mm});
            skCircle(sketch, "E15.14.20.0", {"center": v(-37.14, 191.89) * mm, "radius": 2 * mm});
            skCircle(sketch, "E15.14.21.0", {"center": v(-43.9, 199.26) * mm, "radius": 2 * mm});
            skCircle(sketch, "E15.14.22.0", {"center": v(-50.66, 206.63) * mm, "radius": 2 * mm});
            skCircle(sketch, "E15.14.23.0", {"center": v(-57.42, 214) * mm, "radius": 2 * mm});
            skCircle(sketch, "E15.14.24.0", {"center": v(-64.18, 221.37) * mm, "radius": 2 * mm});
            skCircle(sketch, "E15.15.0.0", {"center": v(105.05, 51.63) * mm, "radius": 2 * mm});
            skCircle(sketch, "E15.15.1.0", {"center": v(98.29, 59) * mm, "radius": 2 * mm});
            skCircle(sketch, "E15.15.2.0", {"center": v(91.53, 66.37) * mm, "radius": 2 * mm});
            skCircle(sketch, "E15.15.3.0", {"center": v(84.77, 73.74) * mm, "radius": 2 * mm});
            skCircle(sketch, "E15.15.4.0", {"center": v(78, 81.11) * mm, "radius": 2 * mm});
            skCircle(sketch, "E15.15.5.0", {"center": v(71.25, 88.48) * mm, "radius": 2 * mm});
            skCircle(sketch, "E15.15.6.0", {"center": v(64.49, 95.85) * mm, "radius": 2 * mm});
            skCircle(sketch, "E15.15.7.0", {"center": v(57.73, 103.22) * mm, "radius": 2 * mm});
            skCircle(sketch, "E15.15.8.0", {"center": v(50.97, 110.59) * mm, "radius": 2 * mm});
            skCircle(sketch, "E15.15.9.0", {"center": v(44.21, 117.96) * mm, "radius": 2 * mm});
            skCircle(sketch, "E15.15.10.0", {"center": v(37.45, 125.33) * mm, "radius": 2 * mm});
            skCircle(sketch, "E15.15.11.0", {"center": v(30.7, 132.7) * mm, "radius": 2 * mm});
            skCircle(sketch, "E15.15.12.0", {"center": v(23.93, 140.07) * mm, "radius": 2 * mm});
            skCircle(sketch, "E15.15.13.0", {"center": v(17.17, 147.44) * mm, "radius": 2 * mm});
            skCircle(sketch, "E15.15.14.0", {"center": v(10.42, 154.8) * mm, "radius": 2 * mm});
            skCircle(sketch, "E15.15.15.0", {"center": v(3.66, 162.18) * mm, "radius": 2 * mm});
            skCircle(sketch, "E15.15.16.0", {"center": v(-3.1, 169.55) * mm, "radius": 2 * mm});
            skCircle(sketch, "E15.15.17.0", {"center": v(-9.86, 176.92) * mm, "radius": 2 * mm});
            skCircle(sketch, "E15.15.18.0", {"center": v(-16.62, 184.29) * mm, "radius": 2 * mm});
            skCircle(sketch, "E15.15.19.0", {"center": v(-23.38, 191.66) * mm, "radius": 2 * mm});
            skCircle(sketch, "E15.15.20.0", {"center": v(-30.14, 199.03) * mm, "radius": 2 * mm});
            skCircle(sketch, "E15.15.21.0", {"center": v(-36.9, 206.4) * mm, "radius": 2 * mm});
            skCircle(sketch, "E15.15.22.0", {"center": v(-43.66, 213.76) * mm, "radius": 2 * mm});
            skCircle(sketch, "E15.15.23.0", {"center": v(-50.42, 221.13) * mm, "radius": 2 * mm});
            skCircle(sketch, "E15.15.24.0", {"center": v(-57.18, 228.5) * mm, "radius": 2 * mm});
            skCircle(sketch, "E15.16.0.0", {"center": v(112.05, 58.77) * mm, "radius": 2 * mm});
            skCircle(sketch, "E15.16.1.0", {"center": v(105.29, 66.14) * mm, "radius": 2 * mm});
            skCircle(sketch, "E15.16.2.0", {"center": v(98.53, 73.5) * mm, "radius": 2 * mm});
            skCircle(sketch, "E15.16.3.0", {"center": v(91.77, 80.88) * mm, "radius": 2 * mm});
            skCircle(sketch, "E15.16.4.0", {"center": v(85.01, 88.25) * mm, "radius": 2 * mm});
            skCircle(sketch, "E15.16.5.0", {"center": v(78.25, 95.62) * mm, "radius": 2 * mm});
            skCircle(sketch, "E15.16.6.0", {"center": v(71.5, 102.99) * mm, "radius": 2 * mm});
            skCircle(sketch, "E15.16.7.0", {"center": v(64.73, 110.36) * mm, "radius": 2 * mm});
            skCircle(sketch, "E15.16.8.0", {"center": v(57.97, 117.73) * mm, "radius": 2 * mm});
            skCircle(sketch, "E15.16.9.0", {"center": v(51.21, 125.1) * mm, "radius": 2 * mm});
            skCircle(sketch, "E15.16.10.0", {"center": v(44.46, 132.47) * mm, "radius": 2 * mm});
            skCircle(sketch, "E15.16.11.0", {"center": v(37.7, 139.84) * mm, "radius": 2 * mm});
            skCircle(sketch, "E15.16.12.0", {"center": v(30.94, 147.2) * mm, "radius": 2 * mm});
            skCircle(sketch, "E15.16.13.0", {"center": v(24.18, 154.58) * mm, "radius": 2 * mm});
            skCircle(sketch, "E15.16.14.0", {"center": v(17.42, 161.95) * mm, "radius": 2 * mm});
            skCircle(sketch, "E15.16.15.0", {"center": v(10.66, 169.32) * mm, "radius": 2 * mm});
            skCircle(sketch, "E15.16.16.0", {"center": v(3.9, 176.68) * mm, "radius": 2 * mm});
            skCircle(sketch, "E15.16.17.0", {"center": v(-2.86, 184.05) * mm, "radius": 2 * mm});
            skCircle(sketch, "E15.16.18.0", {"center": v(-9.62, 191.42) * mm, "radius": 2 * mm});
            skCircle(sketch, "E15.16.19.0", {"center": v(-16.38, 198.8) * mm, "radius": 2 * mm});
            skCircle(sketch, "E15.16.20.0", {"center": v(-23.14, 206.16) * mm, "radius": 2 * mm});
            skCircle(sketch, "E15.16.21.0", {"center": v(-29.9, 213.53) * mm, "radius": 2 * mm});
            skCircle(sketch, "E15.16.22.0", {"center": v(-36.66, 220.9) * mm, "radius": 2 * mm});
            skCircle(sketch, "E15.16.23.0", {"center": v(-43.42, 228.27) * mm, "radius": 2 * mm});
            skCircle(sketch, "E15.16.24.0", {"center": v(-50.17, 235.64) * mm, "radius": 2 * mm});
            skCircle(sketch, "E15.17.0.0", {"center": v(119.05, 65.9) * mm, "radius": 2 * mm});
            skCircle(sketch, "E15.17.1.0", {"center": v(112.3, 73.28) * mm, "radius": 2 * mm});
            skCircle(sketch, "E15.17.2.0", {"center": v(105.53, 80.65) * mm, "radius": 2 * mm});
            skCircle(sketch, "E15.17.3.0", {"center": v(98.77, 88.02) * mm, "radius": 2 * mm});
            skCircle(sketch, "E15.17.4.0", {"center": v(92.01, 95.39) * mm, "radius": 2 * mm});
            skCircle(sketch, "E15.17.5.0", {"center": v(85.26, 102.76) * mm, "radius": 2 * mm});
            skCircle(sketch, "E15.17.6.0", {"center": v(78.5, 110.13) * mm, "radius": 2 * mm});
            skCircle(sketch, "E15.17.7.0", {"center": v(71.74, 117.5) * mm, "radius": 2 * mm});
            skCircle(sketch, "E15.17.8.0", {"center": v(64.98, 124.87) * mm, "radius": 2 * mm});
            skCircle(sketch, "E15.17.9.0", {"center": v(58.22, 132.24) * mm, "radius": 2 * mm});
            skCircle(sketch, "E15.17.10.0", {"center": v(51.46, 139.6) * mm, "radius": 2 * mm});
            skCircle(sketch, "E15.17.11.0", {"center": v(44.7, 146.98) * mm, "radius": 2 * mm});
            skCircle(sketch, "E15.17.12.0", {"center": v(37.94, 154.34) * mm, "radius": 2 * mm});
            skCircle(sketch, "E15.17.13.0", {"center": v(31.18, 161.71) * mm, "radius": 2 * mm});
            skCircle(sketch, "E15.17.14.0", {"center": v(24.42, 169.08) * mm, "radius": 2 * mm});
            skCircle(sketch, "E15.17.15.0", {"center": v(17.66, 176.45) * mm, "radius": 2 * mm});
            skCircle(sketch, "E15.17.16.0", {"center": v(10.9, 183.82) * mm, "radius": 2 * mm});
            skCircle(sketch, "E15.17.17.0", {"center": v(4.14, 191.2) * mm, "radius": 2 * mm});
            skCircle(sketch, "E15.17.18.0", {"center": v(-2.62, 198.56) * mm, "radius": 2 * mm});
            skCircle(sketch, "E15.17.19.0", {"center": v(-9.38, 205.93) * mm, "radius": 2 * mm});
            skCircle(sketch, "E15.17.20.0", {"center": v(-16.13, 213.3) * mm, "radius": 2 * mm});
            skCircle(sketch, "E15.17.21.0", {"center": v(-22.9, 220.67) * mm, "radius": 2 * mm});
            skCircle(sketch, "E15.17.22.0", {"center": v(-29.65, 228.04) * mm, "radius": 2 * mm});
            skCircle(sketch, "E15.17.23.0", {"center": v(-36.41, 235.41) * mm, "radius": 2 * mm});
            skCircle(sketch, "E15.17.24.0", {"center": v(-43.17, 242.78) * mm, "radius": 2 * mm});
            skCircle(sketch, "E15.18.0.0", {"center": v(126.05, 73.05) * mm, "radius": 2 * mm});
            skCircle(sketch, "E15.18.1.0", {"center": v(119.3, 80.42) * mm, "radius": 2 * mm});
            skCircle(sketch, "E15.18.2.0", {"center": v(112.54, 87.79) * mm, "radius": 2 * mm});
            skCircle(sketch, "E15.18.3.0", {"center": v(105.78, 95.16) * mm, "radius": 2 * mm});
            skCircle(sketch, "E15.18.4.0", {"center": v(99.02, 102.53) * mm, "radius": 2 * mm});
            skCircle(sketch, "E15.18.5.0", {"center": v(92.26, 109.9) * mm, "radius": 2 * mm});
            skCircle(sketch, "E15.18.6.0", {"center": v(85.5, 117.27) * mm, "radius": 2 * mm});
            skCircle(sketch, "E15.18.7.0", {"center": v(78.74, 124.63) * mm, "radius": 2 * mm});
            skCircle(sketch, "E15.18.8.0", {"center": v(71.98, 132) * mm, "radius": 2 * mm});
            skCircle(sketch, "E15.18.9.0", {"center": v(65.22, 139.37) * mm, "radius": 2 * mm});
            skCircle(sketch, "E15.18.10.0", {"center": v(58.46, 146.74) * mm, "radius": 2 * mm});
            skCircle(sketch, "E15.18.11.0", {"center": v(51.7, 154.11) * mm, "radius": 2 * mm});
            skCircle(sketch, "E15.18.12.0", {"center": v(44.94, 161.48) * mm, "radius": 2 * mm});
            skCircle(sketch, "E15.18.13.0", {"center": v(38.18, 168.85) * mm, "radius": 2 * mm});
            skCircle(sketch, "E15.18.14.0", {"center": v(31.42, 176.22) * mm, "radius": 2 * mm});
            skCircle(sketch, "E15.18.15.0", {"center": v(24.67, 183.6) * mm, "radius": 2 * mm});
            skCircle(sketch, "E15.18.16.0", {"center": v(17.9, 190.96) * mm, "radius": 2 * mm});
            skCircle(sketch, "E15.18.17.0", {"center": v(11.15, 198.33) * mm, "radius": 2 * mm});
            skCircle(sketch, "E15.18.18.0", {"center": v(4.39, 205.7) * mm, "radius": 2 * mm});
            skCircle(sketch, "E15.18.19.0", {"center": v(-2.37, 213.07) * mm, "radius": 2 * mm});
            skCircle(sketch, "E15.18.20.0", {"center": v(-9.13, 220.44) * mm, "radius": 2 * mm});
            skCircle(sketch, "E15.18.21.0", {"center": v(-15.9, 227.81) * mm, "radius": 2 * mm});
            skCircle(sketch, "E15.18.22.0", {"center": v(-22.65, 235.18) * mm, "radius": 2 * mm});
            skCircle(sketch, "E15.18.23.0", {"center": v(-29.4, 242.55) * mm, "radius": 2 * mm});
            skCircle(sketch, "E15.18.24.0", {"center": v(-36.17, 249.92) * mm, "radius": 2 * mm});
            skCircle(sketch, "E15.19.0.0", {"center": v(133.06, 80.19) * mm, "radius": 2 * mm});
            skCircle(sketch, "E15.19.1.0", {"center": v(126.3, 87.56) * mm, "radius": 2 * mm});
            skCircle(sketch, "E15.19.2.0", {"center": v(119.54, 94.93) * mm, "radius": 2 * mm});
            skCircle(sketch, "E15.19.3.0", {"center": v(112.78, 102.3) * mm, "radius": 2 * mm});
            skCircle(sketch, "E15.19.4.0", {"center": v(106.02, 109.66) * mm, "radius": 2 * mm});
            skCircle(sketch, "E15.19.5.0", {"center": v(99.26, 117.03) * mm, "radius": 2 * mm});
            skCircle(sketch, "E15.19.6.0", {"center": v(92.5, 124.4) * mm, "radius": 2 * mm});
            skCircle(sketch, "E15.19.7.0", {"center": v(85.74, 131.77) * mm, "radius": 2 * mm});
            skCircle(sketch, "E15.19.8.0", {"center": v(78.98, 139.14) * mm, "radius": 2 * mm});
            skCircle(sketch, "E15.19.9.0", {"center": v(72.22, 146.51) * mm, "radius": 2 * mm});
            skCircle(sketch, "E15.19.10.0", {"center": v(65.46, 153.88) * mm, "radius": 2 * mm});
            skCircle(sketch, "E15.19.11.0", {"center": v(58.7, 161.25) * mm, "radius": 2 * mm});
            skCircle(sketch, "E15.19.12.0", {"center": v(51.95, 168.62) * mm, "radius": 2 * mm});
            skCircle(sketch, "E15.19.13.0", {"center": v(45.19, 176) * mm, "radius": 2 * mm});
            skCircle(sketch, "E15.19.14.0", {"center": v(38.43, 183.36) * mm, "radius": 2 * mm});
            skCircle(sketch, "E15.19.15.0", {"center": v(31.67, 190.73) * mm, "radius": 2 * mm});
            skCircle(sketch, "E15.19.16.0", {"center": v(24.9, 198.1) * mm, "radius": 2 * mm});
            skCircle(sketch, "E15.19.17.0", {"center": v(18.15, 205.47) * mm, "radius": 2 * mm});
            skCircle(sketch, "E15.19.18.0", {"center": v(11.4, 212.84) * mm, "radius": 2 * mm});
            skCircle(sketch, "E15.19.19.0", {"center": v(4.63, 220.2) * mm, "radius": 2 * mm});
            skCircle(sketch, "E15.19.20.0", {"center": v(-2.13, 227.58) * mm, "radius": 2 * mm});
            skCircle(sketch, "E15.19.21.0", {"center": v(-8.89, 234.95) * mm, "radius": 2 * mm});
            skCircle(sketch, "E15.19.22.0", {"center": v(-15.65, 242.32) * mm, "radius": 2 * mm});
            skCircle(sketch, "E15.19.23.0", {"center": v(-22.4, 249.69) * mm, "radius": 2 * mm});
            skCircle(sketch, "E15.19.24.0", {"center": v(-29.17, 257.06) * mm, "radius": 2 * mm});
            skCircle(sketch, "E15.20.0.0", {"center": v(140.06, 87.32) * mm, "radius": 2 * mm});
            skCircle(sketch, "E15.20.1.0", {"center": v(133.3, 94.7) * mm, "radius": 2 * mm});
            skCircle(sketch, "E15.20.2.0", {"center": v(126.54, 102.06) * mm, "radius": 2 * mm});
            skCircle(sketch, "E15.20.3.0", {"center": v(119.78, 109.43) * mm, "radius": 2 * mm});
            skCircle(sketch, "E15.20.4.0", {"center": v(113.02, 116.8) * mm, "radius": 2 * mm});
            skCircle(sketch, "E15.20.5.0", {"center": v(106.26, 124.17) * mm, "radius": 2 * mm});
            skCircle(sketch, "E15.20.6.0", {"center": v(99.5, 131.54) * mm, "radius": 2 * mm});
            skCircle(sketch, "E15.20.7.0", {"center": v(92.75, 138.91) * mm, "radius": 2 * mm});
            skCircle(sketch, "E15.20.8.0", {"center": v(85.99, 146.28) * mm, "radius": 2 * mm});
            skCircle(sketch, "E15.20.9.0", {"center": v(79.23, 153.65) * mm, "radius": 2 * mm});
            skCircle(sketch, "E15.20.10.0", {"center": v(72.47, 161.02) * mm, "radius": 2 * mm});
            skCircle(sketch, "E15.20.11.0", {"center": v(65.7, 168.4) * mm, "radius": 2 * mm});
            skCircle(sketch, "E15.20.12.0", {"center": v(58.95, 175.76) * mm, "radius": 2 * mm});
            skCircle(sketch, "E15.20.13.0", {"center": v(52.19, 183.13) * mm, "radius": 2 * mm});
            skCircle(sketch, "E15.20.14.0", {"center": v(45.43, 190.5) * mm, "radius": 2 * mm});
            skCircle(sketch, "E15.20.15.0", {"center": v(38.67, 197.87) * mm, "radius": 2 * mm});
            skCircle(sketch, "E15.20.16.0", {"center": v(31.91, 205.24) * mm, "radius": 2 * mm});
            skCircle(sketch, "E15.20.17.0", {"center": v(25.15, 212.6) * mm, "radius": 2 * mm});
            skCircle(sketch, "E15.20.18.0", {"center": v(18.4, 219.98) * mm, "radius": 2 * mm});
            skCircle(sketch, "E15.20.19.0", {"center": v(11.63, 227.35) * mm, "radius": 2 * mm});
            skCircle(sketch, "E15.20.20.0", {"center": v(4.87, 234.72) * mm, "radius": 2 * mm});
            skCircle(sketch, "E15.20.21.0", {"center": v(-1.88, 242.09) * mm, "radius": 2 * mm});
            skCircle(sketch, "E15.20.22.0", {"center": v(-8.64, 249.46) * mm, "radius": 2 * mm});
            skCircle(sketch, "E15.20.23.0", {"center": v(-15.4, 256.83) * mm, "radius": 2 * mm});
            skCircle(sketch, "E15.20.24.0", {"center": v(-22.16, 264.2) * mm, "radius": 2 * mm});
            skCircle(sketch, "E15.21.0.0", {"center": v(147.06, 94.46) * mm, "radius": 2 * mm});
            skCircle(sketch, "E15.21.1.0", {"center": v(140.3, 101.83) * mm, "radius": 2 * mm});
            skCircle(sketch, "E15.21.2.0", {"center": v(133.55, 109.2) * mm, "radius": 2 * mm});
            skCircle(sketch, "E15.21.3.0", {"center": v(126.79, 116.57) * mm, "radius": 2 * mm});
            skCircle(sketch, "E15.21.4.0", {"center": v(120.03, 123.94) * mm, "radius": 2 * mm});
            skCircle(sketch, "E15.21.5.0", {"center": v(113.27, 131.31) * mm, "radius": 2 * mm});
            skCircle(sketch, "E15.21.6.0", {"center": v(106.5, 138.68) * mm, "radius": 2 * mm});
            skCircle(sketch, "E15.21.7.0", {"center": v(99.75, 146.05) * mm, "radius": 2 * mm});
            skCircle(sketch, "E15.21.8.0", {"center": v(92.99, 153.42) * mm, "radius": 2 * mm});
            skCircle(sketch, "E15.21.9.0", {"center": v(86.23, 160.79) * mm, "radius": 2 * mm});
            skCircle(sketch, "E15.21.10.0", {"center": v(79.47, 168.16) * mm, "radius": 2 * mm});
            skCircle(sketch, "E15.21.11.0", {"center": v(72.71, 175.53) * mm, "radius": 2 * mm});
            skCircle(sketch, "E15.21.12.0", {"center": v(65.95, 182.9) * mm, "radius": 2 * mm});
            skCircle(sketch, "E15.21.13.0", {"center": v(59.2, 190.27) * mm, "radius": 2 * mm});
            skCircle(sketch, "E15.21.14.0", {"center": v(52.43, 197.64) * mm, "radius": 2 * mm});
            skCircle(sketch, "E15.21.15.0", {"center": v(45.67, 205) * mm, "radius": 2 * mm});
            skCircle(sketch, "E15.21.16.0", {"center": v(38.91, 212.38) * mm, "radius": 2 * mm});
            skCircle(sketch, "E15.21.17.0", {"center": v(32.16, 219.75) * mm, "radius": 2 * mm});
            skCircle(sketch, "E15.21.18.0", {"center": v(25.4, 227.12) * mm, "radius": 2 * mm});
            skCircle(sketch, "E15.21.19.0", {"center": v(18.64, 234.49) * mm, "radius": 2 * mm});
            skCircle(sketch, "E15.21.20.0", {"center": v(11.88, 241.86) * mm, "radius": 2 * mm});
            skCircle(sketch, "E15.21.21.0", {"center": v(5.12, 249.23) * mm, "radius": 2 * mm});
            skCircle(sketch, "E15.21.22.0", {"center": v(-1.64, 256.6) * mm, "radius": 2 * mm});
            skCircle(sketch, "E15.21.23.0", {"center": v(-8.4, 263.96) * mm, "radius": 2 * mm});
            skCircle(sketch, "E15.21.24.0", {"center": v(-15.16, 271.33) * mm, "radius": 2 * mm});
            skCircle(sketch, "E15.22.0.0", {"center": v(154.07, 101.6) * mm, "radius": 2 * mm});
            skCircle(sketch, "E15.22.1.0", {"center": v(147.3, 108.97) * mm, "radius": 2 * mm});
            skCircle(sketch, "E15.22.2.0", {"center": v(140.55, 116.34) * mm, "radius": 2 * mm});
            skCircle(sketch, "E15.22.3.0", {"center": v(133.79, 123.71) * mm, "radius": 2 * mm});
            skCircle(sketch, "E15.22.4.0", {"center": v(127.03, 131.08) * mm, "radius": 2 * mm});
            skCircle(sketch, "E15.22.5.0", {"center": v(120.27, 138.45) * mm, "radius": 2 * mm});
            skCircle(sketch, "E15.22.6.0", {"center": v(113.51, 145.82) * mm, "radius": 2 * mm});
            skCircle(sketch, "E15.22.7.0", {"center": v(106.75, 153.19) * mm, "radius": 2 * mm});
            skCircle(sketch, "E15.22.8.0", {"center": v(100, 160.56) * mm, "radius": 2 * mm});
            skCircle(sketch, "E15.22.9.0", {"center": v(93.23, 167.93) * mm, "radius": 2 * mm});
            skCircle(sketch, "E15.22.10.0", {"center": v(86.47, 175.3) * mm, "radius": 2 * mm});
            skCircle(sketch, "E15.22.11.0", {"center": v(79.71, 182.67) * mm, "radius": 2 * mm});
            skCircle(sketch, "E15.22.12.0", {"center": v(72.96, 190.04) * mm, "radius": 2 * mm});
            skCircle(sketch, "E15.22.13.0", {"center": v(66.2, 197.4) * mm, "radius": 2 * mm});
            skCircle(sketch, "E15.22.14.0", {"center": v(59.44, 204.78) * mm, "radius": 2 * mm});
            skCircle(sketch, "E15.22.15.0", {"center": v(52.68, 212.15) * mm, "radius": 2 * mm});
            skCircle(sketch, "E15.22.16.0", {"center": v(45.92, 219.52) * mm, "radius": 2 * mm});
            skCircle(sketch, "E15.22.17.0", {"center": v(39.16, 226.89) * mm, "radius": 2 * mm});
            skCircle(sketch, "E15.22.18.0", {"center": v(32.4, 234.25) * mm, "radius": 2 * mm});
            skCircle(sketch, "E15.22.19.0", {"center": v(25.64, 241.62) * mm, "radius": 2 * mm});
            skCircle(sketch, "E15.22.20.0", {"center": v(18.88, 249) * mm, "radius": 2 * mm});
            skCircle(sketch, "E15.22.21.0", {"center": v(12.12, 256.36) * mm, "radius": 2 * mm});
            skCircle(sketch, "E15.22.22.0", {"center": v(5.36, 263.73) * mm, "radius": 2 * mm});
            skCircle(sketch, "E15.22.23.0", {"center": v(-1.4, 271.1) * mm, "radius": 2 * mm});
            skCircle(sketch, "E15.22.24.0", {"center": v(-8.16, 278.47) * mm, "radius": 2 * mm});
            skCircle(sketch, "E15.23.0.0", {"center": v(161.07, 108.74) * mm, "radius": 2 * mm});
            skCircle(sketch, "E15.23.1.0", {"center": v(154.31, 116.1) * mm, "radius": 2 * mm});
            skCircle(sketch, "E15.23.2.0", {"center": v(147.55, 123.48) * mm, "radius": 2 * mm});
            skCircle(sketch, "E15.23.3.0", {"center": v(140.8, 130.85) * mm, "radius": 2 * mm});
            skCircle(sketch, "E15.23.4.0", {"center": v(134.03, 138.22) * mm, "radius": 2 * mm});
            skCircle(sketch, "E15.23.5.0", {"center": v(127.27, 145.59) * mm, "radius": 2 * mm});
            skCircle(sketch, "E15.23.6.0", {"center": v(120.51, 152.96) * mm, "radius": 2 * mm});
            skCircle(sketch, "E15.23.7.0", {"center": v(113.75, 160.33) * mm, "radius": 2 * mm});
            skCircle(sketch, "E15.23.8.0", {"center": v(107, 167.7) * mm, "radius": 2 * mm});
            skCircle(sketch, "E15.23.9.0", {"center": v(100.24, 175.07) * mm, "radius": 2 * mm});
            skCircle(sketch, "E15.23.10.0", {"center": v(93.48, 182.44) * mm, "radius": 2 * mm});
            skCircle(sketch, "E15.23.11.0", {"center": v(86.72, 189.8) * mm, "radius": 2 * mm});
            skCircle(sketch, "E15.23.12.0", {"center": v(79.96, 197.18) * mm, "radius": 2 * mm});
            skCircle(sketch, "E15.23.13.0", {"center": v(73.2, 204.55) * mm, "radius": 2 * mm});
            skCircle(sketch, "E15.23.14.0", {"center": v(66.44, 211.91) * mm, "radius": 2 * mm});
            skCircle(sketch, "E15.23.15.0", {"center": v(59.68, 219.28) * mm, "radius": 2 * mm});
            skCircle(sketch, "E15.23.16.0", {"center": v(52.92, 226.65) * mm, "radius": 2 * mm});
            skCircle(sketch, "E15.23.17.0", {"center": v(46.16, 234.02) * mm, "radius": 2 * mm});
            skCircle(sketch, "E15.23.18.0", {"center": v(39.4, 241.4) * mm, "radius": 2 * mm});
            skCircle(sketch, "E15.23.19.0", {"center": v(32.64, 248.76) * mm, "radius": 2 * mm});
            skCircle(sketch, "E15.23.20.0", {"center": v(25.88, 256.13) * mm, "radius": 2 * mm});
            skCircle(sketch, "E15.23.21.0", {"center": v(19.12, 263.5) * mm, "radius": 2 * mm});
            skCircle(sketch, "E15.23.22.0", {"center": v(12.37, 270.87) * mm, "radius": 2 * mm});
            skCircle(sketch, "E15.23.23.0", {"center": v(5.6, 278.24) * mm, "radius": 2 * mm});
            skCircle(sketch, "E15.23.24.0", {"center": v(-1.15, 285.61) * mm, "radius": 2 * mm});
            skCircle(sketch, "E15.24.0.0", {"center": v(168.07, 115.88) * mm, "radius": 2 * mm});
            skCircle(sketch, "E15.24.1.0", {"center": v(161.31, 123.25) * mm, "radius": 2 * mm});
            skCircle(sketch, "E15.24.2.0", {"center": v(154.55, 130.62) * mm, "radius": 2 * mm});
            skCircle(sketch, "E15.24.3.0", {"center": v(147.8, 137.99) * mm, "radius": 2 * mm});
            skCircle(sketch, "E15.24.4.0", {"center": v(141.04, 145.36) * mm, "radius": 2 * mm});
            skCircle(sketch, "E15.24.5.0", {"center": v(134.28, 152.73) * mm, "radius": 2 * mm});
            skCircle(sketch, "E15.24.6.0", {"center": v(127.52, 160.1) * mm, "radius": 2 * mm});
            skCircle(sketch, "E15.24.7.0", {"center": v(120.76, 167.47) * mm, "radius": 2 * mm});
            skCircle(sketch, "E15.24.8.0", {"center": v(114, 174.84) * mm, "radius": 2 * mm});
            skCircle(sketch, "E15.24.9.0", {"center": v(107.24, 182.2) * mm, "radius": 2 * mm});
            skCircle(sketch, "E15.24.10.0", {"center": v(100.48, 189.57) * mm, "radius": 2 * mm});
            skCircle(sketch, "E15.24.11.0", {"center": v(93.72, 196.94) * mm, "radius": 2 * mm});
            skCircle(sketch, "E15.24.12.0", {"center": v(86.96, 204.31) * mm, "radius": 2 * mm});
            skCircle(sketch, "E15.24.13.0", {"center": v(80.2, 211.68) * mm, "radius": 2 * mm});
            skCircle(sketch, "E15.24.14.0", {"center": v(73.44, 219.05) * mm, "radius": 2 * mm});
            skCircle(sketch, "E15.24.15.0", {"center": v(66.68, 226.42) * mm, "radius": 2 * mm});
            skCircle(sketch, "E15.24.16.0", {"center": v(59.92, 233.8) * mm, "radius": 2 * mm});
            skCircle(sketch, "E15.24.17.0", {"center": v(53.16, 241.16) * mm, "radius": 2 * mm});
            skCircle(sketch, "E15.24.18.0", {"center": v(46.4, 248.53) * mm, "radius": 2 * mm});
            skCircle(sketch, "E15.24.19.0", {"center": v(39.65, 255.9) * mm, "radius": 2 * mm});
            skCircle(sketch, "E15.24.20.0", {"center": v(32.89, 263.27) * mm, "radius": 2 * mm});
            skCircle(sketch, "E15.24.21.0", {"center": v(26.13, 270.64) * mm, "radius": 2 * mm});
            skCircle(sketch, "E15.24.22.0", {"center": v(19.37, 278.01) * mm, "radius": 2 * mm});
            skCircle(sketch, "E15.24.23.0", {"center": v(12.6, 285.38) * mm, "radius": 2 * mm});
            skCircle(sketch, "E15.24.24.0", {"center": v(5.85, 292.75) * mm, "radius": 2 * mm});
            skLineSegment(sketch, "E15.direction1", {"start": v(0, -55.44) * mm, "end": v(7, -48.3) * mm, "construction": true});
            skLineSegment(sketch, "E15.direction2", {"start": v(0, -55.44) * mm, "end": v(-6.76, -48.08) * mm, "construction": true});
            skSolve(sketch);
        }
        {
            var Q0;
            Q0=qSketchRegion(id+"F29",true);
            extrude(context, id + "F30", {"entities" : qUnion([Q0]), "operationType" : NewBodyOperationType.INTERSECT, "endBound" : BoundingType.SYMMETRIC, "oppositeDirection" : true, "depth" : 155 * mm, "offsetDistance" : 25 * mm});
        }
    });
